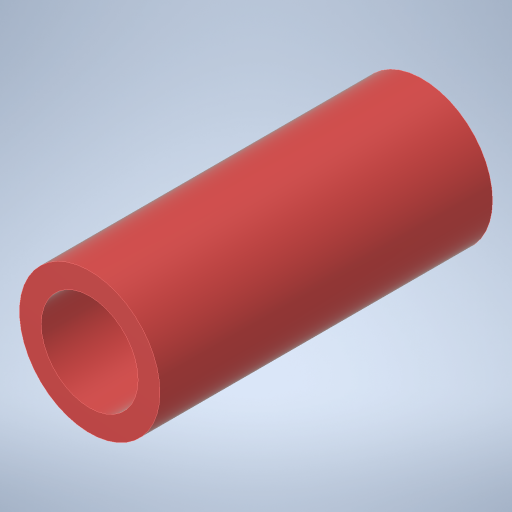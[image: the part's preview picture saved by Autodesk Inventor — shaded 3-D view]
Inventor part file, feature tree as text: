
AUTODESK INVENTOR PART (.ipt)
format: ipt  version: 2023.3 (Build 273359000, 359)  size: 235,008 bytes
history: native  units: in
note: dims shown in document units (in); Inventor stores cm internally (conversion verified against a paired STEP export)
features: extrude x1, sketch x1
ambient origin geometry x8: Origin, YZ Plane, XZ Plane, XY Plane, X Axis, Y Axis, Z Axis, Center Point
bodies: Solid1 (feature_tree)
feature tree (2):
  extrude  "Extrusion1"  [1 undecoded]
  sketch  "Sketch1"  dims[d3=0.0in]
note: 1 required parameter value undecoded (feature->parameter linkage not recoverable at this tier; creation-order binding heuristic only, values carry confidence <= 0.55)
